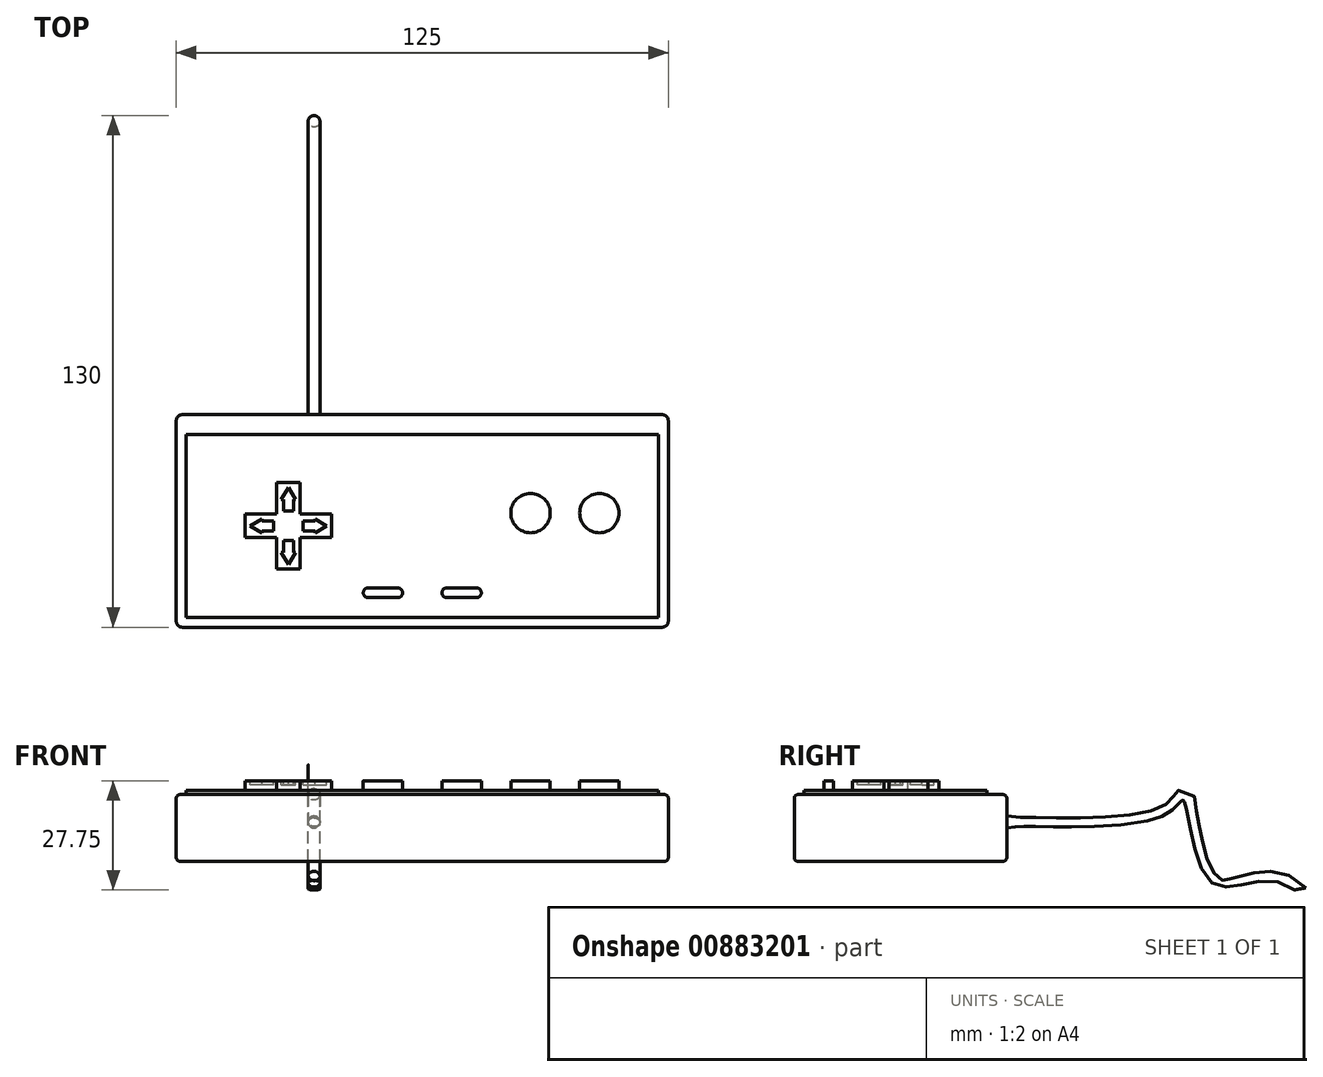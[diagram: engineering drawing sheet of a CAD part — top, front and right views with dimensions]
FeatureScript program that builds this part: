
annotation { "Feature Type Name" : "Feature", "Feature Type Description" : "" }
export const myFeature = defineFeature(function(context is Context, id is Id, definition is map)
    precondition{}
    {
        {
            var Q0;
            Q0=qCreatedBy(makeId("Top.planeOp"),FACE);
            var sketch = newSketch(context, id + "F0", { "sketchPlane" : qUnion([Q0])});
            skLineSegment(sketch, "E0.bottom", {"start": v(-62.5, -27) * mm, "end": v(62.5, -27) * mm});
            skLineSegment(sketch, "E0.top", {"start": v(-62.5, 27) * mm, "end": v(62.5, 27) * mm});
            skLineSegment(sketch, "E0.left", {"start": v(-62.5, -27) * mm, "end": v(-62.5, 27) * mm});
            skLineSegment(sketch, "E0.right", {"start": v(62.5, -27) * mm, "end": v(62.5, 27) * mm});
            skPoint(sketch, "E1", {"position": v(0, 0) * mm});
            skPoint(sketch, "E1.positionSnap0", {"position": v(62.5, 0) * mm});
            skPoint(sketch, "E1.positionSnap1", {"position": v(0, 27) * mm});
            skSolve(sketch);
        }
        {
            var Q0;
            Q0 = qSketchRegion(id + "F0", true);
            extrude(context, id + "F1", {"entities" : qUnion([Q0]), "depth" : 17 * mm, "offsetDistance" : 25 * mm});
        }
        {
            var Q0;
            Q0=makeQuery(id+"F1.opExtrude","SWEPT_FACE",FACE,{"disambiguationData":[OSD([sQuery(id+"F0.wireOp",EDGE,"E0.top")])]});
            var sketch = newSketch(context, id + "F2", { "sketchPlane" : qUnion([Q0])});
            skCircle(sketch, "E2", {"center": v(27.5, 10) * mm, "radius": 1.5 * mm});
            skSolve(sketch);
        }
        {
            var Q0;
            Q0=qCreatedBy(makeId("Right.planeOp"),FACE);
            var Q1;
            Q1=sQuery(id+"F2.wireOp",VERTEX,"E2.center");
            cPlane(context, id + "F3", {"entities" : qUnion([Q0, Q1]), "cplaneType" : CPlaneType.PLANE_POINT, "offset" : 25 * mm, "width" : 150 * mm, "height" : 150 * mm});
        }
        {
            var Q0;
            Q0=qCreatedBy(id+"F3.planeOp",FACE);
            var sketch = newSketch(context, id + "F4", { "sketchPlane" : qUnion([Q0])});
            skFitSpline(sketch, "E3", {"points": [v(27, 8.5) * mm, v(66.54, 11.54) * mm, v(71.99, 15.39) * mm, v(79.3, -5.61) * mm, v(100.05, -7.25) * mm], "startDerivative": vector(12.32, 10.35) * mm, "endDerivative": vector(86.18, -71.5) * mm});
            skSolve(sketch);
        }
        {
            var Q0;
            Q0=makeQuery(id+"F2.imprint","IMPRINT",FACE,{"disambiguationData":[TD([[makeQuery(id+"F2.imprint","IMPRINT",EDGE,{"derivedFrom":sQuery(id+"F2.wireOp",EDGE,"E2")}),1.0]])]});
            var Q1;
            Q1 = qConstructionFilter(qBodyType(qCreatedBy(id + "F4" ,EDGE), BodyType.WIRE), ConstructionObject.NO);
            sweep(context, id + "F5", {"profiles" : qUnion([Q0]), "path" : qUnion([Q1])});
        }
        {
            var Q0;
            Q0=makeQuery(id+"F1.opExtrude","CAP_FACE",FACE,{"disambiguationData":[OSD([sQuery(id+"F0.wireOp",EDGE,"E0.bottom"),sQuery(id+"F0.wireOp",EDGE,"E0.top"),sQuery(id+"F0.wireOp",EDGE,"E0.left"),sQuery(id+"F0.wireOp",EDGE,"E0.right")])],"isStart":false});
            var sketch = newSketch(context, id + "F6", { "sketchPlane" : qUnion([Q0])});
            skLineSegment(sketch, "E4.bottom", {"start": v(-60, 22) * mm, "end": v(60, 22) * mm});
            skLineSegment(sketch, "E4.top", {"start": v(-60, -24.5) * mm, "end": v(60, -24.5) * mm});
            skLineSegment(sketch, "E4.left", {"start": v(-60, 22) * mm, "end": v(-60, -24.5) * mm});
            skLineSegment(sketch, "E4.right", {"start": v(60, 22) * mm, "end": v(60, -24.5) * mm});
            skSolve(sketch);
        }
        {
            var Q0;
            Q0 = qSketchRegion(id + "F6", true);
            extrude(context, id + "F7", {"entities" : qUnion([Q0]), "depth" : 1 * mm, "offsetDistance" : 25 * mm});
        }
        {
            var Q0;
            Q0=makeQuery(id+"F7.opExtrude","CAP_FACE",FACE,{"disambiguationData":[OSD([sQuery(id+"F6.wireOp",EDGE,"E4.bottom"),sQuery(id+"F6.wireOp",EDGE,"E4.top"),sQuery(id+"F6.wireOp",EDGE,"E4.left"),sQuery(id+"F6.wireOp",EDGE,"E4.right")])],"isStart":false});
            var sketch = newSketch(context, id + "F8", { "sketchPlane" : qUnion([Q0])});
            skCircle(sketch, "E5", {"center": v(27.5, 2) * mm, "radius": 5 * mm});
            skCircle(sketch, "E6", {"center": v(45, 2) * mm, "radius": 5 * mm});
            skLineSegment(sketch, "E7", {"start": v(-37, 1.75) * mm, "end": v(-37, 9.75) * mm});
            skLineSegment(sketch, "E8", {"start": v(-37, 9.75) * mm, "end": v(-31, 9.75) * mm});
            skLineSegment(sketch, "E9", {"start": v(-31, 9.75) * mm, "end": v(-31, 1.75) * mm});
            skLineSegment(sketch, "E10", {"start": v(-31, 1.75) * mm, "end": v(-23, 1.75) * mm});
            skLineSegment(sketch, "E11", {"start": v(-23, 1.75) * mm, "end": v(-23, -4.25) * mm});
            skLineSegment(sketch, "E12", {"start": v(-23, -4.25) * mm, "end": v(-31, -4.25) * mm});
            skLineSegment(sketch, "E13", {"start": v(-31, -4.25) * mm, "end": v(-31, -12.25) * mm});
            skLineSegment(sketch, "E14", {"start": v(-31, -12.25) * mm, "end": v(-37, -12.25) * mm});
            skLineSegment(sketch, "E15", {"start": v(-37, -12.25) * mm, "end": v(-37, -4.25) * mm});
            skLineSegment(sketch, "E16", {"start": v(-37, -4.25) * mm, "end": v(-45, -4.25) * mm});
            skLineSegment(sketch, "E17", {"start": v(-45, -4.25) * mm, "end": v(-45, 1.75) * mm});
            skLineSegment(sketch, "E18", {"start": v(-45, 1.75) * mm, "end": v(-37, 1.75) * mm});
            skLineSegment(sketch, "E19.bottom", {"start": v(-15, -17) * mm, "end": v(-5, -17) * mm});
            skLineSegment(sketch, "E19.top", {"start": v(-15, -19.5) * mm, "end": v(-5, -19.5) * mm});
            skLineSegment(sketch, "E19.left", {"start": v(-15, -17) * mm, "end": v(-15, -19.5) * mm});
            skLineSegment(sketch, "E19.right", {"start": v(-5, -17) * mm, "end": v(-5, -19.5) * mm});
            skLineSegment(sketch, "E20.bottom", {"start": v(5, -17) * mm, "end": v(15, -17) * mm});
            skLineSegment(sketch, "E20.top", {"start": v(5, -19.5) * mm, "end": v(15, -19.5) * mm});
            skLineSegment(sketch, "E20.left", {"start": v(5, -17) * mm, "end": v(5, -19.5) * mm});
            skLineSegment(sketch, "E20.right", {"start": v(15, -17) * mm, "end": v(15, -19.5) * mm});
            skSolve(sketch);
        }
        {
            var Q0;
            Q0 = qSketchRegion(id + "F8", true);
            extrude(context, id + "F9", {"entities" : qUnion([Q0]), "depth" : 2.5 * mm, "offsetDistance" : 25 * mm});
        }
        {
            var Q0;
            Q0=makeQuery(id+"F9.opExtrude","CAP_FACE",FACE,{"disambiguationData":[OSD([sQuery(id+"F8.wireOp",EDGE,"E7"),sQuery(id+"F8.wireOp",EDGE,"E8"),sQuery(id+"F8.wireOp",EDGE,"E9"),sQuery(id+"F8.wireOp",EDGE,"E10"),sQuery(id+"F8.wireOp",EDGE,"E11"),sQuery(id+"F8.wireOp",EDGE,"E12"),sQuery(id+"F8.wireOp",EDGE,"E13"),sQuery(id+"F8.wireOp",EDGE,"E14"),sQuery(id+"F8.wireOp",EDGE,"E15"),sQuery(id+"F8.wireOp",EDGE,"E16"),sQuery(id+"F8.wireOp",EDGE,"E17"),sQuery(id+"F8.wireOp",EDGE,"E18")])],"isStart":false});
            var sketch = newSketch(context, id + "F10", { "sketchPlane" : qUnion([Q0])});
            skLineSegment(sketch, "E21", {"start": v(-35.25, 5.5) * mm, "end": v(-35.25, 2.5) * mm});
            skLineSegment(sketch, "E22", {"start": v(-35.25, 2.5) * mm, "end": v(-32.75, 2.5) * mm});
            skLineSegment(sketch, "E23", {"start": v(-32.75, 2.5) * mm, "end": v(-32.75, 5.5) * mm});
            skLineSegment(sketch, "E24", {"start": v(-32.75, 5.5) * mm, "end": v(-32.2, 5.5) * mm});
            skLineSegment(sketch, "E25", {"start": v(-32.2, 5.5) * mm, "end": v(-34, 8.5) * mm});
            skLineSegment(sketch, "E26", {"start": v(-34, 8.5) * mm, "end": v(-35.8, 5.5) * mm});
            skLineSegment(sketch, "E27", {"start": v(-35.8, 5.5) * mm, "end": v(-35.25, 5.5) * mm});
            skPoint(sketch, "E28", {"position": v(-34, -1.25) * mm});
            skPoint(sketch, "E28.positionSnap0", {"position": v(-45, -1.25) * mm});
            skPoint(sketch, "E28.positionSnap1", {"position": v(-34, 2.5) * mm});
            skLineSegment(sketch, "E29.1.0", {"start": v(-37.75, 0) * mm, "end": v(-40.75, 0) * mm});
            skLineSegment(sketch, "E29.1.1", {"start": v(-40.75, 0) * mm, "end": v(-40.75, 0.55) * mm});
            skLineSegment(sketch, "E29.1.2", {"start": v(-40.75, 0.55) * mm, "end": v(-43.75, -1.25) * mm});
            skLineSegment(sketch, "E29.1.3", {"start": v(-43.75, -1.25) * mm, "end": v(-40.75, -3.05) * mm});
            skLineSegment(sketch, "E29.1.4", {"start": v(-40.75, -3.05) * mm, "end": v(-40.75, -2.5) * mm});
            skLineSegment(sketch, "E29.1.5", {"start": v(-40.75, -2.5) * mm, "end": v(-37.75, -2.5) * mm});
            skLineSegment(sketch, "E29.1.6", {"start": v(-37.75, -2.5) * mm, "end": v(-37.75, 0) * mm});
            skLineSegment(sketch, "E29.2.0", {"start": v(-35.25, -5) * mm, "end": v(-35.25, -8) * mm});
            skLineSegment(sketch, "E29.2.1", {"start": v(-35.25, -8) * mm, "end": v(-35.8, -8) * mm});
            skLineSegment(sketch, "E29.2.2", {"start": v(-35.8, -8) * mm, "end": v(-34, -11) * mm});
            skLineSegment(sketch, "E29.2.3", {"start": v(-34, -11) * mm, "end": v(-32.2, -8) * mm});
            skLineSegment(sketch, "E29.2.4", {"start": v(-32.2, -8) * mm, "end": v(-32.75, -8) * mm});
            skLineSegment(sketch, "E29.2.5", {"start": v(-32.75, -8) * mm, "end": v(-32.75, -5) * mm});
            skLineSegment(sketch, "E29.2.6", {"start": v(-32.75, -5) * mm, "end": v(-35.25, -5) * mm});
            skLineSegment(sketch, "E29.3.0", {"start": v(-30.25, -2.5) * mm, "end": v(-27.25, -2.5) * mm});
            skLineSegment(sketch, "E29.3.1", {"start": v(-27.25, -2.5) * mm, "end": v(-27.25, -3.05) * mm});
            skLineSegment(sketch, "E29.3.2", {"start": v(-27.25, -3.05) * mm, "end": v(-24.25, -1.25) * mm});
            skLineSegment(sketch, "E29.3.3", {"start": v(-24.25, -1.25) * mm, "end": v(-27.25, 0.55) * mm});
            skLineSegment(sketch, "E29.3.4", {"start": v(-27.25, 0.55) * mm, "end": v(-27.25, 0) * mm});
            skLineSegment(sketch, "E29.3.5", {"start": v(-27.25, 0) * mm, "end": v(-30.25, 0) * mm});
            skLineSegment(sketch, "E29.3.6", {"start": v(-30.25, 0) * mm, "end": v(-30.25, -2.5) * mm});
            skSolve(sketch);
        }
        {
            var Q0;
            Q0 = qSketchRegion(id + "F10", true);
            extrude(context, id + "F11", {"entities" : qUnion([Q0]), "operationType" : NewBodyOperationType.REMOVE, "oppositeDirection" : true, "depth" : 1 * mm, "offsetDistance" : 25 * mm});
        }
        {
            var Q0;
            Q0=makeQuery(id+"F1.opExtrude","CAP_EDGE",EDGE,{"disambiguationData":[OSD([sQuery(id+"F0.wireOp",EDGE,"E0.bottom")])],"isStart":false});
            var Q1;
            Q1=makeQuery(id+"F1.opExtrude","CAP_EDGE",EDGE,{"disambiguationData":[OSD([sQuery(id+"F0.wireOp",EDGE,"E0.right")])],"isStart":false});
            var Q2;
            Q2=makeQuery(id+"F1.opExtrude","CAP_EDGE",EDGE,{"disambiguationData":[OSD([sQuery(id+"F0.wireOp",EDGE,"E0.top")])],"isStart":false});
            var Q3;
            Q3=makeQuery(id+"F1.opExtrude","CAP_EDGE",EDGE,{"disambiguationData":[OSD([sQuery(id+"F0.wireOp",EDGE,"E0.left")])],"isStart":false});
            var Q4;
            Q4=makeQuery(id+"F1.opExtrude","CAP_EDGE",EDGE,{"disambiguationData":[OSD([sQuery(id+"F0.wireOp",EDGE,"E0.bottom")])],"isStart":true});
            var Q5;
            Q5=makeQuery(id+"F1.opExtrude","CAP_EDGE",EDGE,{"disambiguationData":[OSD([sQuery(id+"F0.wireOp",EDGE,"E0.right")])],"isStart":true});
            var Q6;
            Q6=makeQuery(id+"F1.opExtrude","CAP_EDGE",EDGE,{"disambiguationData":[OSD([sQuery(id+"F0.wireOp",EDGE,"E0.top")])],"isStart":true});
            var Q7;
            Q7=makeQuery(id+"F1.opExtrude","CAP_EDGE",EDGE,{"disambiguationData":[OSD([sQuery(id+"F0.wireOp",EDGE,"E0.left")])],"isStart":true});
            fillet(context, id + "F12", {"entities" : qUnion([Q0, Q1, Q2, Q3, Q4, Q5, Q6, Q7]), "radius" : 1 * mm, "tangentPropagation" : true, "allowEdgeOverflow" : false});
        }
        {
            var Q0;
            Q0=makeQuery(id+"F1.opExtrude","SWEPT_EDGE",EDGE,{"disambiguationData":[OSD([sQuery(id+"F0.wireOp",EDGE,"E0.bottom"),sQuery(id+"F0.wireOp",EDGE,"E0.right")])]});
            var Q1;
            Q1=makeQuery(id+"F1.opExtrude","SWEPT_EDGE",EDGE,{"disambiguationData":[OSD([sQuery(id+"F0.wireOp",EDGE,"E0.top"),sQuery(id+"F0.wireOp",EDGE,"E0.right")])]});
            var Q2;
            Q2=makeQuery(id+"F1.opExtrude","SWEPT_EDGE",EDGE,{"disambiguationData":[OSD([sQuery(id+"F0.wireOp",EDGE,"E0.bottom"),sQuery(id+"F0.wireOp",EDGE,"E0.left")])]});
            var Q3;
            Q3=makeQuery(id+"F1.opExtrude","SWEPT_EDGE",EDGE,{"disambiguationData":[OSD([sQuery(id+"F0.wireOp",EDGE,"E0.top"),sQuery(id+"F0.wireOp",EDGE,"E0.left")])]});
            fillet(context, id + "F13", {"entities" : qUnion([Q0, Q1, Q2, Q3]), "radius" : 1.5 * mm, "tangentPropagation" : true, "allowEdgeOverflow" : false});
        }
        {
            var Q0;
            Q0=makeQuery(id+"F9.opExtrude","SWEPT_EDGE",EDGE,{"disambiguationData":[OSD([sQuery(id+"F8.wireOp",EDGE,"E20.bottom"),sQuery(id+"F8.wireOp",EDGE,"E20.right")])]});
            var Q1;
            Q1=makeQuery(id+"F9.opExtrude","SWEPT_EDGE",EDGE,{"disambiguationData":[OSD([sQuery(id+"F8.wireOp",EDGE,"E20.top"),sQuery(id+"F8.wireOp",EDGE,"E20.right")])]});
            var Q2;
            Q2=makeQuery(id+"F9.opExtrude","SWEPT_EDGE",EDGE,{"disambiguationData":[OSD([sQuery(id+"F8.wireOp",EDGE,"E20.top"),sQuery(id+"F8.wireOp",EDGE,"E20.left")])]});
            var Q3;
            Q3=makeQuery(id+"F9.opExtrude","SWEPT_EDGE",EDGE,{"disambiguationData":[OSD([sQuery(id+"F8.wireOp",EDGE,"E20.bottom"),sQuery(id+"F8.wireOp",EDGE,"E20.left")])]});
            var Q4;
            Q4=makeQuery(id+"F9.opExtrude","SWEPT_EDGE",EDGE,{"disambiguationData":[OSD([sQuery(id+"F8.wireOp",EDGE,"E19.bottom"),sQuery(id+"F8.wireOp",EDGE,"E19.right")])]});
            var Q5;
            Q5=makeQuery(id+"F9.opExtrude","SWEPT_EDGE",EDGE,{"disambiguationData":[OSD([sQuery(id+"F8.wireOp",EDGE,"E19.top"),sQuery(id+"F8.wireOp",EDGE,"E19.right")])]});
            var Q6;
            Q6=makeQuery(id+"F9.opExtrude","SWEPT_EDGE",EDGE,{"disambiguationData":[OSD([sQuery(id+"F8.wireOp",EDGE,"E19.top"),sQuery(id+"F8.wireOp",EDGE,"E19.left")])]});
            var Q7;
            Q7=makeQuery(id+"F9.opExtrude","SWEPT_EDGE",EDGE,{"disambiguationData":[OSD([sQuery(id+"F8.wireOp",EDGE,"E19.bottom"),sQuery(id+"F8.wireOp",EDGE,"E19.left")])]});
            fillet(context, id + "F14", {"entities" : qUnion([Q0, Q1, Q2, Q3, Q4, Q5, Q6, Q7]), "radius" : 1.25 * mm, "tangentPropagation" : true, "allowEdgeOverflow" : false});
        }
    });
